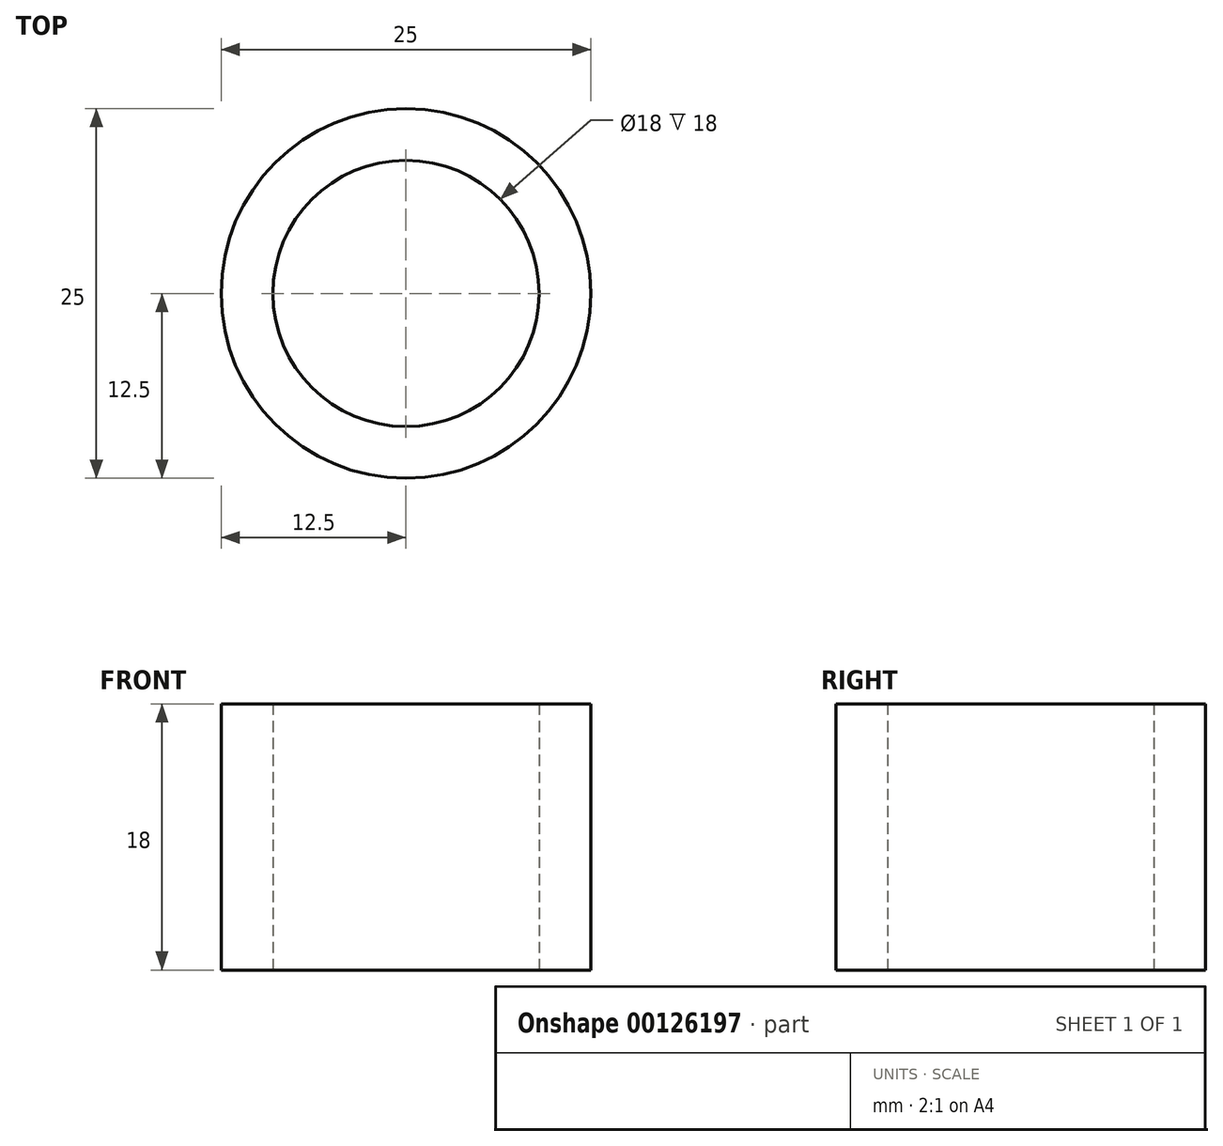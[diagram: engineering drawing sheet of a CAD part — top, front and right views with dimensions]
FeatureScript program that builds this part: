
annotation { "Feature Type Name" : "Feature", "Feature Type Description" : "" }
export const myFeature = defineFeature(function(context is Context, id is Id, definition is map)
    precondition{}
    {
        {
            var Q0;
            Q0=qCreatedBy(makeId("Top.planeOp"),FACE);
            var sketch = newSketch(context, id + "F0", { "sketchPlane" : qUnion([Q0])});
            skCircle(sketch, "E0", {"center": v(0, 0) * mm, "radius": 12.5 * mm});
            skCircle(sketch, "E1", {"center": v(0, 0) * mm, "radius": 9 * mm});
            skSolve(sketch);
        }
        {
            var Q0;
            Q0=makeQuery(id+"F0.imprint","IMPRINT",FACE,{"disambiguationData":[TD([[makeQuery(id+"F0.imprint","IMPRINT",EDGE,{"derivedFrom":sQuery(id+"F0.wireOp",EDGE,"E0")}),1.0]])]});
            extrude(context, id + "F1", {"entities" : qUnion([Q0]), "depth" : 18 * mm});
        }
    });
